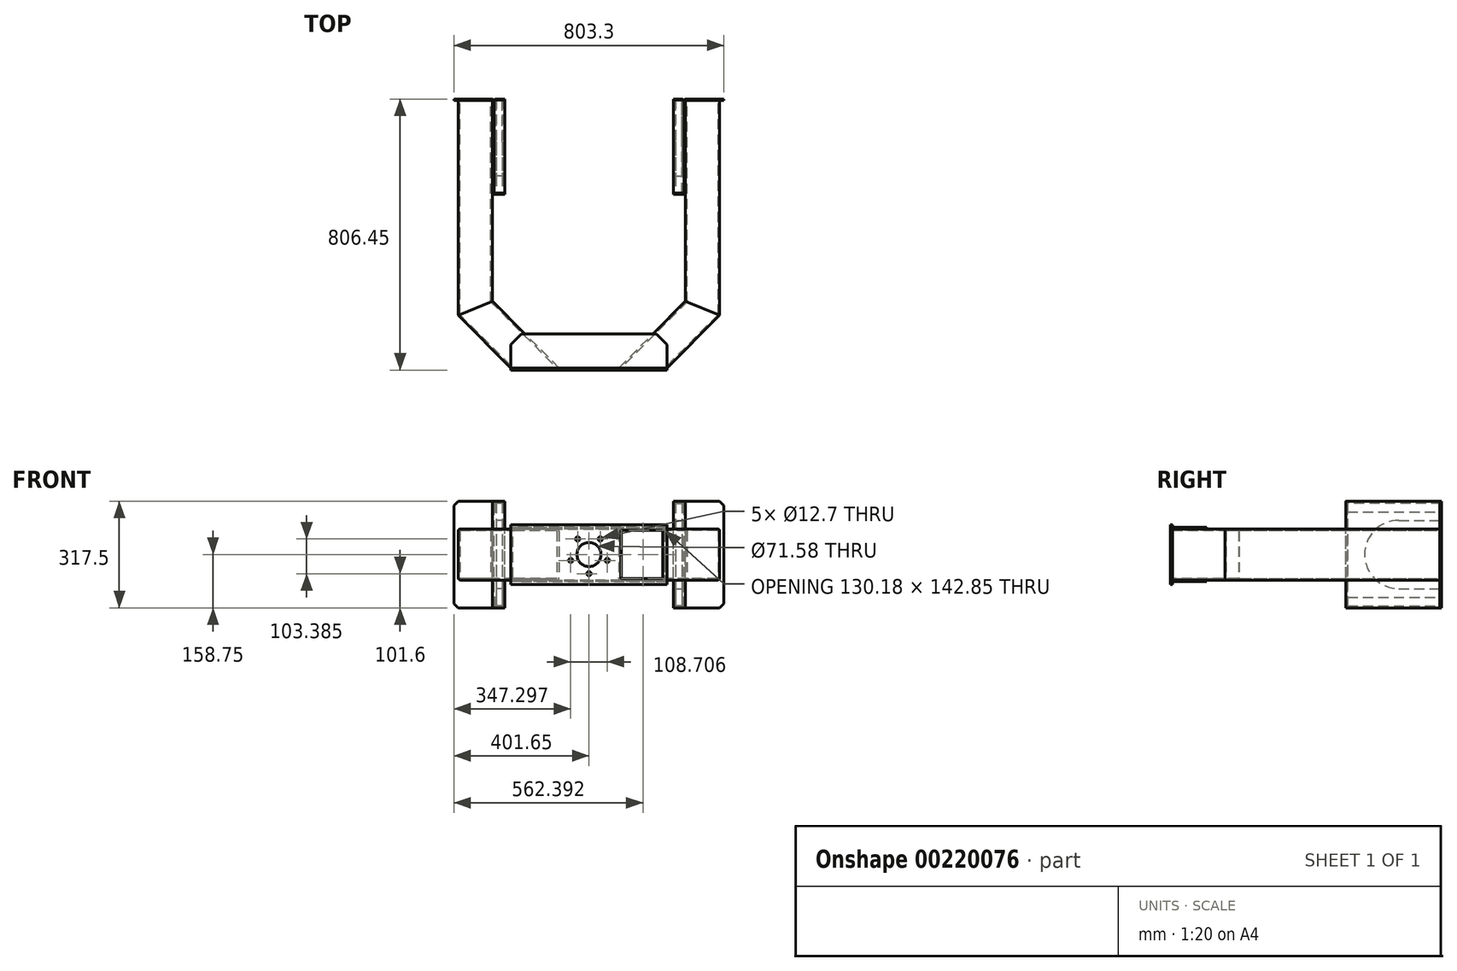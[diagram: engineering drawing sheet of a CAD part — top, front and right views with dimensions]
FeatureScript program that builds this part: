
annotation { "Feature Type Name" : "Feature", "Feature Type Description" : "" }
export const myFeature = defineFeature(function(context is Context, id is Id, definition is map)
    precondition{}
    {
        {
            var Q0;
            Q0=qCreatedBy(makeId("Right.planeOp"),FACE);
            cPlane(context, id + "F0", {"entities" : qUnion([Q0]), "cplaneType" : CPlaneType.OFFSET, "offset" : 276.22 * mm, "width" : 152.4 * mm, "height" : 152.4 * mm});
        }
        {
            var Q0;
            Q0=qCreatedBy(makeId("Front.planeOp"),FACE);
            cPlane(context, id + "F1", {"entities" : qUnion([Q0]), "cplaneType" : CPlaneType.OFFSET, "offset" : 679.45 * mm, "oppositeDirection" : true, "width" : 152.4 * mm, "height" : 152.4 * mm});
        }
        {
            var Q0;
            Q0=qCreatedBy(id+"F0.planeOp",FACE);
            var sketch = newSketch(context, id + "F2", { "sketchPlane" : qUnion([Q0])});
            skLineSegment(sketch, "E0", {"start": v(-327.65, 0) * mm, "end": v(926.93, 0) * mm, "construction": true});
            skLineSegment(sketch, "E1", {"start": v(679.45, -237.46) * mm, "end": v(679.45, 292.03) * mm, "construction": true});
            skLineSegment(sketch, "E2.bottom", {"start": v(806.45, 152.4) * mm, "end": v(527.05, 152.4) * mm});
            skLineSegment(sketch, "E2.top", {"start": v(806.45, -152.4) * mm, "end": v(527.05, -152.4) * mm});
            skLineSegment(sketch, "E2.right", {"start": v(527.05, 152.4) * mm, "end": v(527.05, -152.4) * mm});
            skPoint(sketch, "E2.middle", {"position": v(679.45, 0) * mm});
            skArc(sketch, "E3", {"start": v(679.45, 101.6) * mm, "mid": v(577.85, 0) * mm, "end": v(679.45, -101.6) * mm});
            skLineSegment(sketch, "E4", {"start": v(679.45, 101.6) * mm, "end": v(806.45, 101.6) * mm});
            skLineSegment(sketch, "E5", {"start": v(679.45, -101.6) * mm, "end": v(806.45, -101.6) * mm});
            skLineSegment(sketch, "E6", {"start": v(806.45, 152.4) * mm, "end": v(806.45, 101.6) * mm});
            skPoint(sketch, "E2.left.start.orphan", {"position": v(831.85, 152.4) * mm});
            skLineSegment(sketch, "E7.trimOffspring", {"start": v(806.45, -101.6) * mm, "end": v(806.45, -152.4) * mm});
            skPoint(sketch, "E8.orphan", {"position": v(831.85, -152.4) * mm});
            skSolve(sketch);
        }
        {
            var Q0;
            Q0 = qSketchRegion(id + "F2", true);
            extrude(context, id + "F3", {"entities" : qUnion([Q0]), "oppositeDirection" : true, "depth" : 18.29 * mm});
        }
        {
            var Q0;
            Q0=makeQuery(id+"F3.opExtrude","SWEPT_BODY",BODY,{"disambiguationData":[OSD([sQuery(id+"F2.wireOp",EDGE,"E2.bottom"),sQuery(id+"F2.wireOp",EDGE,"E2.top"),sQuery(id+"F2.wireOp",EDGE,"E2.right"),sQuery(id+"F2.wireOp",EDGE,"E3"),sQuery(id+"F2.wireOp",EDGE,"E4"),sQuery(id+"F2.wireOp",EDGE,"E5"),sQuery(id+"F2.wireOp",EDGE,"E6"),sQuery(id+"F2.wireOp",EDGE,"E7.trimOffspring")])]});
            var Q1;
            Q1=qCreatedBy(makeId("Right.planeOp"),FACE);
            mirror(context, id + "F4", {"entities" : qUnion([Q0]), "mirrorPlane" : qUnion([Q1])});
        }
        {
            var Q0;
            Q0=qCreatedBy(makeId("Front.planeOp"),FACE);
            var sketch = newSketch(context, id + "F5", { "sketchPlane" : qUnion([Q0])});
            skLineSegment(sketch, "E9.bottom", {"start": v(232.59, 88.9) * mm, "end": v(-232.59, 88.9) * mm});
            skLineSegment(sketch, "E9.top", {"start": v(232.59, -88.9) * mm, "end": v(-232.59, -88.9) * mm});
            skLineSegment(sketch, "E9.left", {"start": v(232.59, 88.9) * mm, "end": v(232.59, -88.9) * mm});
            skLineSegment(sketch, "E9.right", {"start": v(-232.59, 88.9) * mm, "end": v(-232.59, -88.9) * mm});
            skPoint(sketch, "E9.middle", {"position": v(0, 0) * mm});
            skCircle(sketch, "E10", {"center": v(0, 0) * mm, "radius": 35.79 * mm});
            skCircle(sketch, "E11", {"center": v(0, 0) * mm, "radius": 57.15 * mm, "construction": true});
            skLineSegment(sketch, "E12", {"start": v(0, 0) * mm, "end": v(0, 133.78) * mm, "construction": true});
            skCircle(sketch, "E13", {"center": v(0, 0) * mm, "radius": 76.68 * mm, "construction": true});
            skLineSegment(sketch, "E14", {"start": v(0, 0) * mm, "end": v(0, -130.52) * mm, "construction": true});
            skCircle(sketch, "E15", {"center": v(0, -57.15) * mm, "radius": 6.35 * mm});
            skCircle(sketch, "E16.1.0", {"center": v(54.35, -17.66) * mm, "radius": 6.35 * mm});
            skCircle(sketch, "E16.2.0", {"center": v(33.6, 46.24) * mm, "radius": 6.35 * mm});
            skCircle(sketch, "E16.3.0", {"center": v(-33.6, 46.24) * mm, "radius": 6.35 * mm});
            skCircle(sketch, "E16.4.0", {"center": v(-54.35, -17.66) * mm, "radius": 6.35 * mm});
            skSolve(sketch);
        }
        {
            var Q0;
            Q0 = qSketchRegion(id + "F5", true);
            extrude(context, id + "F6", {"entities" : qUnion([Q0]), "oppositeDirection" : true, "depth" : 6.35 * mm});
        }
        {
            var Q0;
            Q0=makeQuery(id+"F3.opExtrude","SWEPT_FACE",FACE,{"disambiguationData":[OSD([sQuery(id+"F2.wireOp",EDGE,"E6")])]});
            var sketch = newSketch(context, id + "F7", { "sketchPlane" : qUnion([Q0])});
            skLineSegment(sketch, "E17.0", {"start": v(-276.23, 152.4) * mm, "end": v(-276.23, 127) * mm});
            skLineSegment(sketch, "E18", {"start": v(-282.58, 158.75) * mm, "end": v(-282.58, 127) * mm});
            skLineSegment(sketch, "E19.0", {"start": v(-276.23, -127) * mm, "end": v(-276.23, -152.4) * mm});
            skLineSegment(sketch, "E20", {"start": v(-282.58, -127) * mm, "end": v(-282.58, -158.75) * mm});
            skLineSegment(sketch, "E21", {"start": v(-282.58, -158.75) * mm, "end": v(-250.83, -158.75) * mm});
            skLineSegment(sketch, "E22", {"start": v(-282.58, -127) * mm, "end": v(-276.23, -127) * mm});
            skLineSegment(sketch, "E23", {"start": v(-250.83, -152.4) * mm, "end": v(-250.83, -158.75) * mm});
            skPoint(sketch, "E24.0.start.orphan", {"position": v(-276.23, -101.6) * mm});
            skLineSegment(sketch, "E25", {"start": v(-276.23, -152.4) * mm, "end": v(-250.83, -152.4) * mm});
            skLineSegment(sketch, "E26", {"start": v(-282.58, 127) * mm, "end": v(-276.23, 127) * mm});
            skLineSegment(sketch, "E27", {"start": v(-250.83, 158.75) * mm, "end": v(-250.83, 152.4) * mm});
            skLineSegment(sketch, "E28", {"start": v(-276.23, 152.4) * mm, "end": v(-250.83, 152.4) * mm});
            skLineSegment(sketch, "E29", {"start": v(-282.58, 158.75) * mm, "end": v(-250.83, 158.75) * mm});
            skSolve(sketch);
        }
        {
            var Q0;
            Q0 = qSketchRegion(id + "F7", true);
            var Q1;
            Q1=makeQuery(id+"F3.opExtrude","SWEPT_FACE",FACE,{"disambiguationData":[OSD([sQuery(id+"F2.wireOp",EDGE,"E2.right")])]});
            extrude(context, id + "F8", {"entities" : qUnion([Q0]), "endBound" : BoundingType.UP_TO_SURFACE, "oppositeDirection" : true, "endBoundEntityFace" : qUnion([Q1]), "depth" : 25.4 * mm});
        }
        {
            var Q0;
            Q0=makeQuery(id+"F8.opExtrude","SWEPT_EDGE",EDGE,{"disambiguationData":[OSD([sQuery(id+"F7.wireOp",EDGE,"E19.0"),sQuery(id+"F7.wireOp",EDGE,"E25")])]});
            var Q1;
            Q1=makeQuery(id+"F8.opExtrude","SWEPT_EDGE",EDGE,{"disambiguationData":[OSD([sQuery(id+"F7.wireOp",EDGE,"E17.0"),sQuery(id+"F7.wireOp",EDGE,"E28")])]});
            fillet(context, id + "F9", {"entities" : qUnion([Q0, Q1]), "radius" : 2.3 * mm, "tangentPropagation" : true, "allowEdgeOverflow" : false});
        }
        {
            var Q0;
            Q0=makeQuery(id+"F8.opExtrude","SWEPT_EDGE",EDGE,{"disambiguationData":[OSD([sQuery(id+"F7.wireOp",EDGE,"E18"),sQuery(id+"F7.wireOp",EDGE,"E29")])]});
            var Q1;
            Q1=makeQuery(id+"F8.opExtrude","SWEPT_EDGE",EDGE,{"disambiguationData":[OSD([sQuery(id+"F7.wireOp",EDGE,"E20"),sQuery(id+"F7.wireOp",EDGE,"E21")])]});
            fillet(context, id + "F10", {"entities" : qUnion([Q0, Q1]), "radius" : 8.64 * mm, "tangentPropagation" : true, "allowEdgeOverflow" : false});
        }
        {
            var Q0;
            Q0=makeQuery(id+"F8.opExtrude","TWEAK_EDGE",EDGE,{"derivedFrom":[makeQuery(id+"F3.opExtrude","SWEPT_FACE",FACE,{"disambiguationData":[OSD([sQuery(id+"F2.wireOp",EDGE,"E2.right")])]}),makeQuery(id+"F7.imprint","IMPRINT",EDGE,{"derivedFrom":sQuery(id+"F7.wireOp",EDGE,"E29")})]});
            var Q1;
            Q1=makeQuery(id+"F8.opExtrude","CAP_EDGE",EDGE,{"disambiguationData":[OSD([sQuery(id+"F7.wireOp",EDGE,"E29")])],"isStart":true});
            var Q2;
            Q2=makeQuery(id+"F8.opExtrude","TWEAK_EDGE",EDGE,{"derivedFrom":[makeQuery(id+"F3.opExtrude","SWEPT_FACE",FACE,{"disambiguationData":[OSD([sQuery(id+"F2.wireOp",EDGE,"E2.right")])]}),makeQuery(id+"F7.imprint","IMPRINT",EDGE,{"derivedFrom":sQuery(id+"F7.wireOp",EDGE,"E21")})]});
            var Q3;
            Q3=makeQuery(id+"F8.opExtrude","CAP_EDGE",EDGE,{"disambiguationData":[OSD([sQuery(id+"F7.wireOp",EDGE,"E20")])],"isStart":true});
            chamfer(context, id + "F11", {"entities" : qUnion([Q0, Q1, Q2, Q3]), "width" : 3.17 * mm, "tangentPropagation" : true});
        }
        {
            var Q0;
            Q0=makeQuery(id+"F8.opExtrude","SWEPT_FACE",FACE,{"disambiguationData":[OSD([sQuery(id+"F7.wireOp",EDGE,"E29")])]});
            var sketch = newSketch(context, id + "F12", { "sketchPlane" : qUnion([Q0])});
            skLineSegment(sketch, "E30.0", {"start": v(282.58, 799.39) * mm, "end": v(282.58, 529.34) * mm});
            skLineSegment(sketch, "E31", {"start": v(289.64, 806.45) * mm, "end": v(401.65, 806.45) * mm});
            skLineSegment(sketch, "E32", {"start": v(289.64, 801.67) * mm, "end": v(401.65, 801.67) * mm});
            skLineSegment(sketch, "E33", {"start": v(287.35, 799.39) * mm, "end": v(287.35, 529.34) * mm});
            skPoint(sketch, "E34.visualSharp", {"position": v(287.35, 801.67) * mm});
            skArc(sketch, "E34.filletArc", {"start": v(289.64, 801.67) * mm, "mid": v(288.02, 801) * mm, "end": v(287.35, 799.39) * mm});
            skPoint(sketch, "E35.visualSharp", {"position": v(282.58, 806.45) * mm});
            skArc(sketch, "E35.filletArc", {"start": v(289.64, 806.45) * mm, "mid": v(284.64, 804.38) * mm, "end": v(282.58, 799.39) * mm});
            skLineSegment(sketch, "E36", {"start": v(401.65, 806.45) * mm, "end": v(401.65, 801.67) * mm});
            skLineSegment(sketch, "E37", {"start": v(250.83, 522.27) * mm, "end": v(280.29, 522.27) * mm});
            skPoint(sketch, "E38.visualSharp", {"position": v(282.58, 527.05) * mm});
            skArc(sketch, "E38.filletArc", {"start": v(280.29, 527.05) * mm, "mid": v(281.9, 527.72) * mm, "end": v(282.58, 529.34) * mm});
            skPoint(sketch, "E39.visualSharp", {"position": v(287.35, 522.27) * mm});
            skArc(sketch, "E39.filletArc", {"start": v(280.29, 522.27) * mm, "mid": v(285.28, 524.34) * mm, "end": v(287.35, 529.34) * mm});
            skLineSegment(sketch, "E40.0", {"start": v(280.29, 527.05) * mm, "end": v(250.83, 527.05) * mm});
            skLineSegment(sketch, "E41", {"start": v(250.83, 527.05) * mm, "end": v(250.83, 522.27) * mm});
            skPoint(sketch, "E42.orphan", {"position": v(273.94, 527.05) * mm});
            skSolve(sketch);
        }
        {
            var Q0;
            Q0 = qSketchRegion(id + "F12", true);
            var Q1;
            Q1=makeQuery(id+"F8.opExtrude","SWEPT_FACE",FACE,{"disambiguationData":[OSD([sQuery(id+"F7.wireOp",EDGE,"E21")])]});
            extrude(context, id + "F13", {"entities" : qUnion([Q0]), "oppositeDirection" : true, "endBoundEntityFace" : qUnion([Q1]), "depth" : 317.5 * mm});
        }
        {
            var Q0;
            Q0=makeQuery(id+"F13.opExtrude","CAP_EDGE",EDGE,{"disambiguationData":[OSD([sQuery(id+"F12.wireOp",EDGE,"E36")])],"isStart":true});
            var Q1;
            Q1=makeQuery(id+"F13.opExtrude","CAP_EDGE",EDGE,{"disambiguationData":[OSD([sQuery(id+"F12.wireOp",EDGE,"E36")])],"isStart":false});
            chamfer(context, id + "F14", {"entities" : qUnion([Q0, Q1]), "width" : 12.7 * mm, "tangentPropagation" : true});
        }
        {
            var Q0;
            Q0=makeQuery(id+"F8.opExtrude","SWEPT_BODY",BODY,{"disambiguationData":[OSD([sQuery(id+"F7.wireOp",EDGE,"E17.0"),sQuery(id+"F7.wireOp",EDGE,"E18"),sQuery(id+"F7.wireOp",EDGE,"E26"),sQuery(id+"F7.wireOp",EDGE,"E27"),sQuery(id+"F7.wireOp",EDGE,"E28"),sQuery(id+"F7.wireOp",EDGE,"E29")])]});
            var Q1;
            Q1=makeQuery(id+"F8.opExtrude","SWEPT_BODY",BODY,{"disambiguationData":[OSD([sQuery(id+"F7.wireOp",EDGE,"E19.0"),sQuery(id+"F7.wireOp",EDGE,"E20"),sQuery(id+"F7.wireOp",EDGE,"E21"),sQuery(id+"F7.wireOp",EDGE,"E22"),sQuery(id+"F7.wireOp",EDGE,"E23"),sQuery(id+"F7.wireOp",EDGE,"E25")])]});
            var Q2;
            Q2=makeQuery(id+"F13.opExtrude","SWEPT_BODY",BODY,{"disambiguationData":[OSD([sQuery(id+"F12.wireOp",EDGE,"E30.0"),sQuery(id+"F12.wireOp",EDGE,"E31"),sQuery(id+"F12.wireOp",EDGE,"E32"),sQuery(id+"F12.wireOp",EDGE,"E33"),sQuery(id+"F12.wireOp",EDGE,"E34.filletArc"),sQuery(id+"F12.wireOp",EDGE,"E35.filletArc"),sQuery(id+"F12.wireOp",EDGE,"E36"),sQuery(id+"F12.wireOp",EDGE,"E37"),sQuery(id+"F12.wireOp",EDGE,"E38.filletArc"),sQuery(id+"F12.wireOp",EDGE,"E39.filletArc"),sQuery(id+"F12.wireOp",EDGE,"E40.0"),sQuery(id+"F12.wireOp",EDGE,"E41")])]});
            var Q3;
            Q3=qCreatedBy(makeId("Right.planeOp"),FACE);
            mirror(context, id + "F15", {"entities" : qUnion([Q0, Q1, Q2]), "mirrorPlane" : qUnion([Q3])});
        }
        {
            var Q0;
            Q0=makeQuery(id+"F13.opExtrude","SWEPT_FACE",FACE,{"disambiguationData":[OSD([sQuery(id+"F12.wireOp",EDGE,"E32")])]});
            var sketch = newSketch(context, id + "F16", { "sketchPlane" : qUnion([Q0])});
            skLineSegment(sketch, "E43", {"start": v(-134.32, 0) * mm, "end": v(598.37, 0) * mm, "construction": true});
            skLineSegment(sketch, "E44.0", {"start": v(287.35, -69.14) * mm, "end": v(287.35, 69.14) * mm, "construction": true});
            skLineSegment(sketch, "E45.bottom", {"start": v(294.41, 76.2) * mm, "end": v(381.89, 76.2) * mm});
            skLineSegment(sketch, "E45.top", {"start": v(294.41, -76.2) * mm, "end": v(381.89, -76.2) * mm});
            skLineSegment(sketch, "E45.left", {"start": v(287.35, 69.14) * mm, "end": v(287.35, -69.14) * mm});
            skLineSegment(sketch, "E45.right", {"start": v(388.95, 69.14) * mm, "end": v(388.95, -69.14) * mm});
            skPoint(sketch, "E45.middle", {"position": v(338.15, 0) * mm});
            skPoint(sketch, "E46.visualSharp", {"position": v(388.95, 76.2) * mm});
            skArc(sketch, "E46.filletArc", {"start": v(388.95, 69.14) * mm, "mid": v(386.88, 74.13) * mm, "end": v(381.89, 76.2) * mm});
            skPoint(sketch, "E47.visualSharp", {"position": v(388.95, -76.2) * mm});
            skArc(sketch, "E47.filletArc", {"start": v(381.89, -76.2) * mm, "mid": v(386.88, -74.13) * mm, "end": v(388.95, -69.14) * mm});
            skPoint(sketch, "E48.newPointA", {"position": v(287.35, -158.75) * mm});
            skPoint(sketch, "E48.newPointB", {"position": v(287.35, -76.2) * mm});
            skArc(sketch, "E48.filletArc", {"start": v(287.35, -69.14) * mm, "mid": v(289.42, -74.13) * mm, "end": v(294.41, -76.2) * mm});
            skPoint(sketch, "E49.newPointA", {"position": v(287.35, 158.75) * mm});
            skPoint(sketch, "E49.newPointB", {"position": v(287.35, 76.2) * mm});
            skArc(sketch, "E49.filletArc", {"start": v(294.41, 76.2) * mm, "mid": v(289.42, 74.13) * mm, "end": v(287.35, 69.14) * mm});
            skLineSegment(sketch, "E50.bottom", {"start": v(294.41, 71.42) * mm, "end": v(381.89, 71.42) * mm});
            skLineSegment(sketch, "E50.top", {"start": v(294.41, -71.42) * mm, "end": v(381.89, -71.42) * mm});
            skLineSegment(sketch, "E50.left", {"start": v(292.13, 69.14) * mm, "end": v(292.13, -69.14) * mm});
            skLineSegment(sketch, "E50.right", {"start": v(384.18, 69.14) * mm, "end": v(384.18, -69.14) * mm});
            skPoint(sketch, "E51.visualSharp", {"position": v(384.18, -71.42) * mm});
            skArc(sketch, "E51.filletArc", {"start": v(381.89, -71.42) * mm, "mid": v(383.5, -70.76) * mm, "end": v(384.18, -69.14) * mm});
            skPoint(sketch, "E52.visualSharp", {"position": v(292.13, -71.42) * mm});
            skArc(sketch, "E52.filletArc", {"start": v(292.13, -69.14) * mm, "mid": v(292.8, -70.76) * mm, "end": v(294.41, -71.42) * mm});
            skPoint(sketch, "E53.visualSharp", {"position": v(292.13, 71.42) * mm});
            skArc(sketch, "E53.filletArc", {"start": v(294.41, 71.42) * mm, "mid": v(292.8, 70.76) * mm, "end": v(292.13, 69.14) * mm});
            skPoint(sketch, "E54.visualSharp", {"position": v(384.18, 71.42) * mm});
            skArc(sketch, "E54.filletArc", {"start": v(384.18, 69.14) * mm, "mid": v(383.5, 70.76) * mm, "end": v(381.89, 71.42) * mm});
            skSolve(sketch);
        }
        {
            var Q0;
            Q0 = qSketchRegion(id + "F16", true);
            var Q1;
            Q1=makeQuery(id+"F6.opExtrude","CAP_FACE",FACE,{"disambiguationData":[OSD([sQuery(id+"F5.wireOp",EDGE,"E9.bottom"),sQuery(id+"F5.wireOp",EDGE,"E9.top"),sQuery(id+"F5.wireOp",EDGE,"E9.left"),sQuery(id+"F5.wireOp",EDGE,"E9.right"),sQuery(id+"F5.wireOp",EDGE,"E10"),sQuery(id+"F5.wireOp",EDGE,"E15"),sQuery(id+"F5.wireOp",EDGE,"E16.1.0"),sQuery(id+"F5.wireOp",EDGE,"E16.2.0"),sQuery(id+"F5.wireOp",EDGE,"E16.3.0"),sQuery(id+"F5.wireOp",EDGE,"E16.4.0")])],"isStart":false});
            extrude(context, id + "F17", {"entities" : qUnion([Q0]), "endBound" : BoundingType.UP_TO_SURFACE, "endBoundEntityFace" : qUnion([Q1]), "depth" : 25.4 * mm});
        }
        {
            var Q0;
            Q0=makeQuery(id+"F17.opExtrude","SWEPT_FACE",FACE,{"disambiguationData":[OSD([sQuery(id+"F16.wireOp",EDGE,"E45.bottom")])]});
            var sketch = newSketch(context, id + "F18", { "sketchPlane" : qUnion([Q0])});
            skLineSegment(sketch, "E55.0", {"start": v(388.95, 6.35) * mm, "end": v(388.95, 162.71) * mm});
            skLineSegment(sketch, "E56.0", {"start": v(287.35, 6.35) * mm, "end": v(287.35, 204.8) * mm});
            skLineSegment(sketch, "E57", {"start": v(287.35, 204.8) * mm, "end": v(388.95, 162.71) * mm});
            skLineSegment(sketch, "E58", {"start": v(287.35, 6.35) * mm, "end": v(388.95, 6.35) * mm});
            skPoint(sketch, "E59.orphan", {"position": v(388.95, 801.67) * mm});
            skPoint(sketch, "E60.orphan", {"position": v(287.35, 801.67) * mm});
            skSolve(sketch);
        }
        {
            var Q0;
            Q0 = qSketchRegion(id + "F18", true);
            extrude(context, id + "F19", {"entities" : qUnion([Q0]), "operationType" : NewBodyOperationType.REMOVE, "endBound" : BoundingType.THROUGH_ALL, "oppositeDirection" : true, "depth" : 25.4 * mm});
        }
        {
            var Q0;
            Q0=makeQuery(id+"F17.opExtrude","SWEPT_BODY",BODY,{"disambiguationData":[OSD([sQuery(id+"F16.wireOp",EDGE,"E45.bottom"),sQuery(id+"F16.wireOp",EDGE,"E45.top"),sQuery(id+"F16.wireOp",EDGE,"E45.left"),sQuery(id+"F16.wireOp",EDGE,"E45.right"),sQuery(id+"F16.wireOp",EDGE,"E46.filletArc"),sQuery(id+"F16.wireOp",EDGE,"E47.filletArc"),sQuery(id+"F16.wireOp",EDGE,"E48.filletArc"),sQuery(id+"F16.wireOp",EDGE,"E49.filletArc"),sQuery(id+"F16.wireOp",EDGE,"E50.bottom"),sQuery(id+"F16.wireOp",EDGE,"E50.top"),sQuery(id+"F16.wireOp",EDGE,"E50.left"),sQuery(id+"F16.wireOp",EDGE,"E50.right"),sQuery(id+"F16.wireOp",EDGE,"E51.filletArc"),sQuery(id+"F16.wireOp",EDGE,"E52.filletArc"),sQuery(id+"F16.wireOp",EDGE,"E53.filletArc"),sQuery(id+"F16.wireOp",EDGE,"E54.filletArc")])]});
            var Q1;
            Q1=qCreatedBy(makeId("Right.planeOp"),FACE);
            mirror(context, id + "F20", {"entities" : qUnion([Q0]), "mirrorPlane" : qUnion([Q1])});
        }
        {
            var Q0;
            Q0=qCreatedBy(makeId("Top.planeOp"),FACE);
            var sketch = newSketch(context, id + "F21", { "sketchPlane" : qUnion([Q0])});
            skLineSegment(sketch, "E61", {"start": v(0, 447.22) * mm, "end": v(0, -3.22) * mm, "construction": true});
            skLineSegment(sketch, "E62.0", {"start": v(388.95, 6.35) * mm, "end": v(388.95, 801.67) * mm, "construction": true});
            skLineSegment(sketch, "E63.0", {"start": v(287.35, 6.35) * mm, "end": v(287.35, 801.67) * mm, "construction": true});
            skLineSegment(sketch, "E64", {"start": v(88.9, 6.35) * mm, "end": v(232.58, 6.35) * mm});
            skLineSegment(sketch, "E65", {"start": v(-232.59, 6.35) * mm, "end": v(-35.79, 6.35) * mm, "construction": true});
            skLineSegment(sketch, "E66", {"start": v(88.9, 392.15) * mm, "end": v(88.9, -106.28) * mm, "construction": true});
            skLineSegment(sketch, "E67", {"start": v(88.9, 6.35) * mm, "end": v(287.35, 204.8) * mm});
            skLineSegment(sketch, "E68", {"start": v(232.58, 6.35) * mm, "end": v(388.95, 162.72) * mm});
            skLineSegment(sketch, "E69", {"start": v(388.95, 162.72) * mm, "end": v(287.35, 204.8) * mm});
            skPoint(sketch, "E70.orphan", {"position": v(35.79, 6.35) * mm});
            skPoint(sketch, "E71.orphan", {"position": v(232.59, 6.35) * mm});
            skSolve(sketch);
        }
        {
            var Q0;
            Q0 = qSketchRegion(id + "F21", true);
            extrude(context, id + "F22", {"entities" : qUnion([Q0]), "endBound" : BoundingType.SYMMETRIC, "depth" : 152.4 * mm});
        }
        {
            var Q0;
            Q0=makeQuery(id+"F22.opExtrude","CAP_EDGE",EDGE,{"disambiguationData":[OSD([sQuery(id+"F21.wireOp",EDGE,"E68")])],"isStart":false});
            var Q1;
            Q1=makeQuery(id+"F22.opExtrude","CAP_EDGE",EDGE,{"disambiguationData":[OSD([sQuery(id+"F21.wireOp",EDGE,"E67")])],"isStart":false});
            var Q2;
            Q2=makeQuery(id+"F22.opExtrude","CAP_EDGE",EDGE,{"disambiguationData":[OSD([sQuery(id+"F21.wireOp",EDGE,"E68")])],"isStart":true});
            var Q3;
            Q3=makeQuery(id+"F22.opExtrude","CAP_EDGE",EDGE,{"disambiguationData":[OSD([sQuery(id+"F21.wireOp",EDGE,"E67")])],"isStart":true});
            fillet(context, id + "F23", {"entities" : qUnion([Q0, Q1, Q2, Q3]), "radius" : 7.06 * mm, "tangentPropagation" : true, "allowEdgeOverflow" : false});
        }
        {
            var Q0;
            Q0=makeQuery(id+"F22.opExtrude","SWEPT_FACE",FACE,{"disambiguationData":[OSD([sQuery(id+"F21.wireOp",EDGE,"E69")])]});
            shell(context, id + "F24", {"entities" : qUnion([Q0]), "thickness" : 4.78 * mm});
        }
        {
            var Q0;
            Q0=makeQuery(id+"F22.opExtrude","SWEPT_EDGE",EDGE,{"disambiguationData":[OSD([sQuery(id+"F21.wireOp",EDGE,"E64"),sQuery(id+"F21.wireOp",EDGE,"E67")])]});
            cPlane(context, id + "F25", {"entities" : qUnion([Q0]), "cplaneType" : CPlaneType.LINE_ANGLE, "offset" : 25.4 * mm, "angle" : 135 * degree, "width" : 152.4 * mm, "height" : 152.4 * mm});
        }
        {
            var Q0;
            Q0=qCreatedBy(id+"F25.planeOp",FACE);
            var sketch = newSketch(context, id + "F26", { "sketchPlane" : qUnion([Q0])});
            skLineSegment(sketch, "E72.0.0", {"start": v(-63.15, -69.14) * mm, "end": v(-63.15, 69.14) * mm});
            skArc(sketch, "E72.0.1", {"start": v(-65.43, 71.42) * mm, "mid": v(-63.82, 70.76) * mm, "end": v(-63.15, 69.14) * mm});
            skLineSegment(sketch, "E72.0.2", {"start": v(-65.43, 71.42) * mm, "end": v(-152.91, 71.42) * mm});
            skArc(sketch, "E72.0.3", {"start": v(-155.2, 69.14) * mm, "mid": v(-154.53, 70.76) * mm, "end": v(-152.91, 71.42) * mm});
            skLineSegment(sketch, "E72.0.4", {"start": v(-155.2, 69.14) * mm, "end": v(-155.2, -69.14) * mm});
            skArc(sketch, "E72.0.5", {"start": v(-152.91, -71.42) * mm, "mid": v(-154.53, -70.76) * mm, "end": v(-155.2, -69.14) * mm});
            skLineSegment(sketch, "E72.0.6", {"start": v(-152.91, -71.42) * mm, "end": v(-65.43, -71.42) * mm});
            skArc(sketch, "E72.0.7", {"start": v(-63.15, -69.14) * mm, "mid": v(-63.82, -70.76) * mm, "end": v(-65.43, -71.42) * mm});
            skSolve(sketch);
        }
        {
            var Q0;
            Q0 = qSketchRegion(id + "F26", true);
            extrude(context, id + "F27", {"entities" : qUnion([Q0]), "operationType" : NewBodyOperationType.REMOVE, "depth" : 228.6 * mm});
        }
        {
            var Q0;
            Q0=makeQuery(id+"F22.opExtrude","SWEPT_BODY",BODY,{"disambiguationData":[OSD([sQuery(id+"F21.wireOp",EDGE,"E64"),sQuery(id+"F21.wireOp",EDGE,"E67"),sQuery(id+"F21.wireOp",EDGE,"E68"),sQuery(id+"F21.wireOp",EDGE,"E69")])]});
            var Q1;
            Q1=qCreatedBy(makeId("Right.planeOp"),FACE);
            mirror(context, id + "F28", {"entities" : qUnion([Q0]), "mirrorPlane" : qUnion([Q1])});
        }
        {
            var Q0;
            Q0=makeQuery(id+"F22.opExtrude","CAP_FACE",FACE,{"disambiguationData":[OSD([sQuery(id+"F21.wireOp",EDGE,"E64"),sQuery(id+"F21.wireOp",EDGE,"E67"),sQuery(id+"F21.wireOp",EDGE,"E68"),sQuery(id+"F21.wireOp",EDGE,"E69")])],"isStart":false});
            var sketch = newSketch(context, id + "F29", { "sketchPlane" : qUnion([Q0])});
            skLineSegment(sketch, "E73.0", {"start": v(232.59, 6.35) * mm, "end": v(-232.59, 6.35) * mm});
            skLineSegment(sketch, "E74.0", {"start": v(232.59, 6.35) * mm, "end": v(232.58, 6.35) * mm});
            skLineSegment(sketch, "E75", {"start": v(-232.58, 107.95) * mm, "end": v(232.59, 107.95) * mm});
            skPoint(sketch, "E76.orphan", {"position": v(-388.95, 162.72) * mm});
            skPoint(sketch, "E77.orphan", {"position": v(388.95, 162.72) * mm});
            skLineSegment(sketch, "E78", {"start": v(-232.58, 6.35) * mm, "end": v(-232.58, 107.95) * mm});
            skLineSegment(sketch, "E79", {"start": v(232.59, 6.35) * mm, "end": v(232.59, 107.95) * mm});
            skSolve(sketch);
        }
        {
            var Q0;
            Q0 = qSketchRegion(id + "F29", true);
            extrude(context, id + "F30", {"entities" : qUnion([Q0]), "depth" : 4.78 * mm});
        }
        {
            var Q0;
            Q0=makeQuery(id+"F22.opExtrude","CAP_FACE",FACE,{"disambiguationData":[OSD([sQuery(id+"F21.wireOp",EDGE,"E64"),sQuery(id+"F21.wireOp",EDGE,"E67"),sQuery(id+"F21.wireOp",EDGE,"E68"),sQuery(id+"F21.wireOp",EDGE,"E69")])],"isStart":true});
            var sketch = newSketch(context, id + "F31", { "sketchPlane" : qUnion([Q0])});
            skLineSegment(sketch, "E80.0", {"start": v(232.59, -6.35) * mm, "end": v(-232.59, -6.35) * mm});
            skLineSegment(sketch, "E81.0", {"start": v(232.58, -6.35) * mm, "end": v(232.59, -6.35) * mm});
            skLineSegment(sketch, "E82", {"start": v(-232.58, -107.95) * mm, "end": v(232.59, -107.95) * mm});
            skPoint(sketch, "E83.orphan", {"position": v(-388.95, -162.72) * mm});
            skPoint(sketch, "E84.orphan", {"position": v(388.95, -162.72) * mm});
            skLineSegment(sketch, "E85", {"start": v(232.59, -6.35) * mm, "end": v(232.59, -107.95) * mm});
            skLineSegment(sketch, "E86", {"start": v(-232.58, -6.35) * mm, "end": v(-232.58, -107.95) * mm});
            skSolve(sketch);
        }
        {
            var Q0;
            Q0 = qSketchRegion(id + "F31", true);
            extrude(context, id + "F32", {"entities" : qUnion([Q0]), "depth" : 4.78 * mm});
        }
        {
            var Q0;
            {var subQ0=sQuery(id+"F21.wireOp",EDGE,"E67");Q0=makeQuery(id+"F23.opFillet","BLEND_EDGE",EDGE,{"blendedFrom":[makeQuery(id+"F22.opExtrude","CAP_EDGE",EDGE,{"disambiguationData":[OSD([subQ0])],"isStart":false}),makeQuery(id+"F22.opExtrude","CAP_FACE",FACE,{"disambiguationData":[OSD([sQuery(id+"F21.wireOp",EDGE,"E64"),subQ0,sQuery(id+"F21.wireOp",EDGE,"E68"),sQuery(id+"F21.wireOp",EDGE,"E69")])],"isStart":false})],"blendedInto":[makeQuery(id+"F22.opExtrude","CAP_FACE",FACE,{"disambiguationData":[OSD([sQuery(id+"F21.wireOp",EDGE,"E64"),subQ0,sQuery(id+"F21.wireOp",EDGE,"E68"),sQuery(id+"F21.wireOp",EDGE,"E69")])],"isStart":false})]});}
            var Q1;
            Q1=makeQuery(id+"F30.opExtrude","SWEPT_EDGE",EDGE,{"disambiguationData":[OSD([sQuery(id+"F29.wireOp",EDGE,"E75"),sQuery(id+"F29.wireOp",EDGE,"E79")])]});
            var Q2;
            Q2=makeQuery(id+"F30.opExtrude","SWEPT_EDGE",EDGE,{"disambiguationData":[OSD([sQuery(id+"F29.wireOp",EDGE,"E75"),sQuery(id+"F29.wireOp",EDGE,"E78")])]});
            var Q3;
            Q3=makeQuery(id+"F32.opExtrude","SWEPT_EDGE",EDGE,{"disambiguationData":[OSD([sQuery(id+"F31.wireOp",EDGE,"E82"),sQuery(id+"F31.wireOp",EDGE,"E86")])]});
            var Q4;
            Q4=makeQuery(id+"F32.opExtrude","SWEPT_EDGE",EDGE,{"disambiguationData":[OSD([sQuery(id+"F31.wireOp",EDGE,"E82"),sQuery(id+"F31.wireOp",EDGE,"E85")])]});
            chamfer(context, id + "F33", {"entities" : qUnion([Q0, Q1, Q2, Q3, Q4]), "width" : 31.75 * mm, "tangentPropagation" : true});
        }
    });
